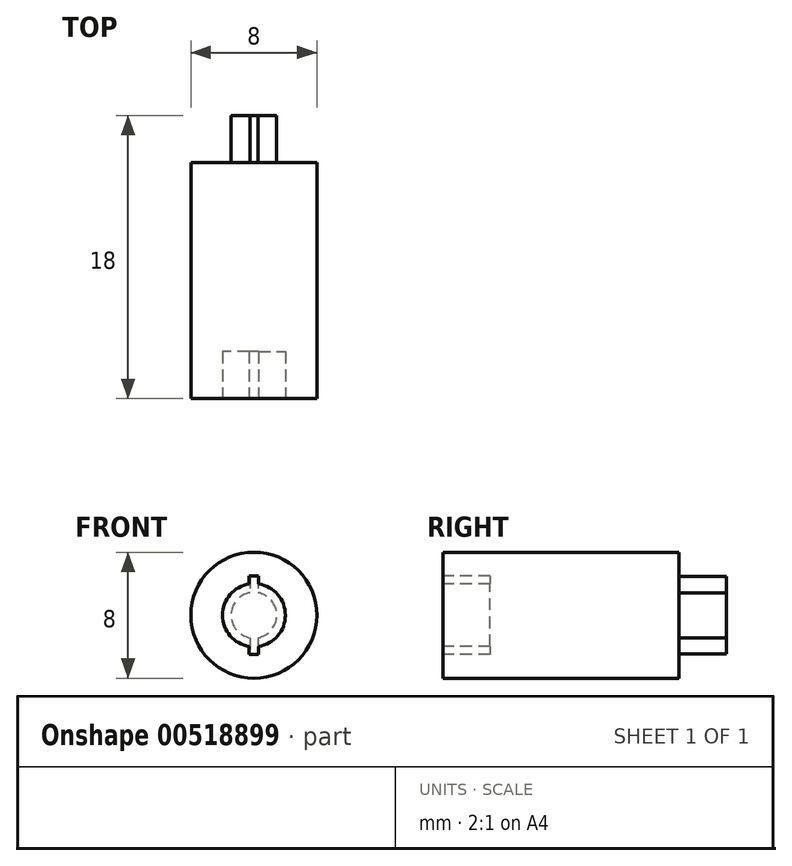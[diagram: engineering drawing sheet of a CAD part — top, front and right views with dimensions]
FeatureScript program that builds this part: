
annotation { "Feature Type Name" : "Feature", "Feature Type Description" : "" }
export const myFeature = defineFeature(function(context is Context, id is Id, definition is map)
    precondition{}
    {
        {
            var Q0;
            Q0=qCreatedBy(makeId("Front.planeOp"),FACE);
            var sketch = newSketch(context, id + "F0", { "sketchPlane" : qUnion([Q0])});
            skCircle(sketch, "E0", {"center": v(0, 0) * mm, "radius": 2 * mm});
            skPoint(sketch, "E1", {"position": v(1.25, -1.56) * mm});
            skLineSegment(sketch, "E2.bottom", {"start": v(0.3, 2.5) * mm, "end": v(-0.3, 2.5) * mm});
            skLineSegment(sketch, "E2.top", {"start": v(0.3, -2.5) * mm, "end": v(-0.3, -2.5) * mm});
            skLineSegment(sketch, "E2.left", {"start": v(0.3, 2.5) * mm, "end": v(0.3, -2.5) * mm});
            skLineSegment(sketch, "E2.right", {"start": v(-0.3, 2.5) * mm, "end": v(-0.3, -2.5) * mm});
            skCircle(sketch, "E3", {"center": v(0, 0) * mm, "radius": 4 * mm});
            skSolve(sketch);
        }
        {
            var Q0;
            Q0 = qSketchRegion(id + "F0", true);
            var Q1;
            {var subQ0=sQuery(id+"F0.wireOp",EDGE,"E2.left");var subQ1=sQuery(id+"F0.wireOp",EDGE,"E0");var subQ2=makeQuery(id+"F0.imprint","INTERSECT",VERTEX,{"disambiguationData":[OD(0.0)],"derivedFrom":[subQ1,subQ0]});Q1=makeQuery(id+"F0.imprint","IMPRINT",FACE,{"disambiguationData":[TD([[makeQuery(id+"F0.imprint","IMPRINT",EDGE,{"disambiguationData":[TD([[subQ2,1.0]])],"derivedFrom":subQ1}),1.0]])]});}
            var Q2;
            {var subQ0=sQuery(id+"F0.wireOp",EDGE,"E2.right");var subQ1=sQuery(id+"F0.wireOp",EDGE,"E0");var subQ2=makeQuery(id+"F0.imprint","INTERSECT",VERTEX,{"disambiguationData":[OD(0.0)],"derivedFrom":[subQ1,subQ0]});Q2=makeQuery(id+"F0.imprint","IMPRINT",FACE,{"disambiguationData":[TD([[makeQuery(id+"F0.imprint","IMPRINT",EDGE,{"disambiguationData":[TD([[subQ2,-1.0]])],"derivedFrom":subQ1}),1.0]])]});}
            var Q3;
            {var subQ0=sQuery(id+"F0.wireOp",EDGE,"E2.right");var subQ1=sQuery(id+"F0.wireOp",EDGE,"E0");var subQ2=makeQuery(id+"F0.imprint","INTERSECT",VERTEX,{"disambiguationData":[OD(0.0)],"derivedFrom":[subQ1,subQ0]});Q3=makeQuery(id+"F0.imprint","IMPRINT",FACE,{"disambiguationData":[TD([[makeQuery(id+"F0.imprint","IMPRINT",EDGE,{"disambiguationData":[TD([[subQ2,1.0]])],"derivedFrom":subQ1}),1.0]])]});}
            var Q4;
            {var subQ5=sQuery(id+"F0.wireOp",EDGE,"E2.bottom");Q4=makeQuery(id+"F0.imprint","IMPRINT",FACE,{"disambiguationData":[TD([[makeQuery(id+"F0.imprint","IMPRINT",EDGE,{"derivedFrom":subQ5}),1.0]])]});}
            var Q5;
            {var subQ5=sQuery(id+"F0.wireOp",EDGE,"E2.top");Q5=makeQuery(id+"F0.imprint","IMPRINT",FACE,{"disambiguationData":[TD([[makeQuery(id+"F0.imprint","IMPRINT",EDGE,{"derivedFrom":subQ5}),-1.0]])]});}
            extrude(context, id + "F1", {"entities" : qUnion([Q0, Q1, Q2, Q3, Q4, Q5]), "oppositeDirection" : true, "depth" : 15 * mm, "offsetDistance" : 25 * mm});
        }
        {
            var Q0;
            {var subQ0=sQuery(id+"F0.wireOp",EDGE,"E2.right");var subQ1=sQuery(id+"F0.wireOp",EDGE,"E0");var subQ2=makeQuery(id+"F0.imprint","INTERSECT",VERTEX,{"disambiguationData":[OD(0.0)],"derivedFrom":[subQ1,subQ0]});Q0=makeQuery(id+"F0.imprint","IMPRINT",FACE,{"disambiguationData":[TD([[makeQuery(id+"F0.imprint","IMPRINT",EDGE,{"disambiguationData":[TD([[subQ2,1.0]])],"derivedFrom":subQ1}),1.0]])]});}
            var Q1;
            {var subQ0=sQuery(id+"F0.wireOp",EDGE,"E2.left");var subQ1=sQuery(id+"F0.wireOp",EDGE,"E0");var subQ2=makeQuery(id+"F0.imprint","INTERSECT",VERTEX,{"disambiguationData":[OD(0.0)],"derivedFrom":[subQ1,subQ0]});Q1=makeQuery(id+"F0.imprint","IMPRINT",FACE,{"disambiguationData":[TD([[makeQuery(id+"F0.imprint","IMPRINT",EDGE,{"disambiguationData":[TD([[subQ2,1.0]])],"derivedFrom":subQ1}),1.0]])]});}
            var Q2;
            {var subQ5=sQuery(id+"F0.wireOp",EDGE,"E2.bottom");Q2=makeQuery(id+"F0.imprint","IMPRINT",FACE,{"disambiguationData":[TD([[makeQuery(id+"F0.imprint","IMPRINT",EDGE,{"derivedFrom":subQ5}),1.0]])]});}
            var Q3;
            {var subQ0=sQuery(id+"F0.wireOp",EDGE,"E2.right");var subQ1=sQuery(id+"F0.wireOp",EDGE,"E0");var subQ2=makeQuery(id+"F0.imprint","INTERSECT",VERTEX,{"disambiguationData":[OD(0.0)],"derivedFrom":[subQ1,subQ0]});Q3=makeQuery(id+"F0.imprint","IMPRINT",FACE,{"disambiguationData":[TD([[makeQuery(id+"F0.imprint","IMPRINT",EDGE,{"disambiguationData":[TD([[subQ2,-1.0]])],"derivedFrom":subQ1}),1.0]])]});}
            var Q4;
            {var subQ5=sQuery(id+"F0.wireOp",EDGE,"E2.top");Q4=makeQuery(id+"F0.imprint","IMPRINT",FACE,{"disambiguationData":[TD([[makeQuery(id+"F0.imprint","IMPRINT",EDGE,{"derivedFrom":subQ5}),-1.0]])]});}
            extrude(context, id + "F2", {"entities" : qUnion([Q0, Q1, Q2, Q3, Q4]), "operationType" : NewBodyOperationType.REMOVE, "oppositeDirection" : true, "depth" : 3 * mm, "offsetDistance" : 25 * mm});
        }
        {
            var Q0;
            Q0=makeQuery(id+"F1.opExtrude","CAP_FACE",FACE,{"disambiguationData":[OSD([sQuery(id+"F0.wireOp",EDGE,"E3")])],"isStart":false});
            var sketch = newSketch(context, id + "F3", { "sketchPlane" : qUnion([Q0])});
            skCircle(sketch, "E4", {"center": v(0, 0) * mm, "radius": 1.45 * mm});
            skLineSegment(sketch, "E5.bottom", {"start": v(0.25, 2.45) * mm, "end": v(-0.25, 2.45) * mm});
            skLineSegment(sketch, "E5.top", {"start": v(0.25, -2.45) * mm, "end": v(-0.25, -2.45) * mm});
            skLineSegment(sketch, "E5.left", {"start": v(0.25, 2.45) * mm, "end": v(0.25, -2.45) * mm});
            skLineSegment(sketch, "E5.right", {"start": v(-0.25, 2.45) * mm, "end": v(-0.25, -2.45) * mm});
            skSolve(sketch);
        }
        {
            var Q0;
            {var subQ0=sQuery(id+"F3.wireOp",EDGE,"E5.right");var subQ1=sQuery(id+"F3.wireOp",EDGE,"E4");var subQ2=makeQuery(id+"F3.imprint","INTERSECT",VERTEX,{"disambiguationData":[OD(0.0)],"derivedFrom":[subQ1,subQ0]});Q0=makeQuery(id+"F3.imprint","IMPRINT",FACE,{"disambiguationData":[TD([[makeQuery(id+"F3.imprint","IMPRINT",EDGE,{"disambiguationData":[TD([[subQ2,-1.0]])],"derivedFrom":subQ1}),1.0]])]});}
            var Q1;
            {var subQ0=sQuery(id+"F3.wireOp",EDGE,"E5.right");var subQ1=sQuery(id+"F3.wireOp",EDGE,"E4");var subQ2=makeQuery(id+"F3.imprint","INTERSECT",VERTEX,{"disambiguationData":[OD(0.0)],"derivedFrom":[subQ1,subQ0]});Q1=makeQuery(id+"F3.imprint","IMPRINT",FACE,{"disambiguationData":[TD([[makeQuery(id+"F3.imprint","IMPRINT",EDGE,{"disambiguationData":[TD([[subQ2,1.0]])],"derivedFrom":subQ1}),1.0]])]});}
            var Q2;
            {var subQ0=sQuery(id+"F3.wireOp",EDGE,"E5.left");var subQ1=sQuery(id+"F3.wireOp",EDGE,"E4");var subQ2=makeQuery(id+"F3.imprint","INTERSECT",VERTEX,{"disambiguationData":[OD(0.0)],"derivedFrom":[subQ1,subQ0]});Q2=makeQuery(id+"F3.imprint","IMPRINT",FACE,{"disambiguationData":[TD([[makeQuery(id+"F3.imprint","IMPRINT",EDGE,{"disambiguationData":[TD([[subQ2,1.0]])],"derivedFrom":subQ1}),1.0]])]});}
            var Q3;
            {var subQ5=sQuery(id+"F3.wireOp",EDGE,"E5.bottom");Q3=makeQuery(id+"F3.imprint","IMPRINT",FACE,{"disambiguationData":[TD([[makeQuery(id+"F3.imprint","IMPRINT",EDGE,{"derivedFrom":subQ5}),1.0]])]});}
            var Q4;
            {var subQ5=sQuery(id+"F3.wireOp",EDGE,"E5.top");Q4=makeQuery(id+"F3.imprint","IMPRINT",FACE,{"disambiguationData":[TD([[makeQuery(id+"F3.imprint","IMPRINT",EDGE,{"derivedFrom":subQ5}),-1.0]])]});}
            extrude(context, id + "F4", {"entities" : qUnion([Q0, Q1, Q2, Q3, Q4]), "operationType" : NewBodyOperationType.ADD, "depth" : 3 * mm, "offsetDistance" : 25 * mm});
        }
    });
